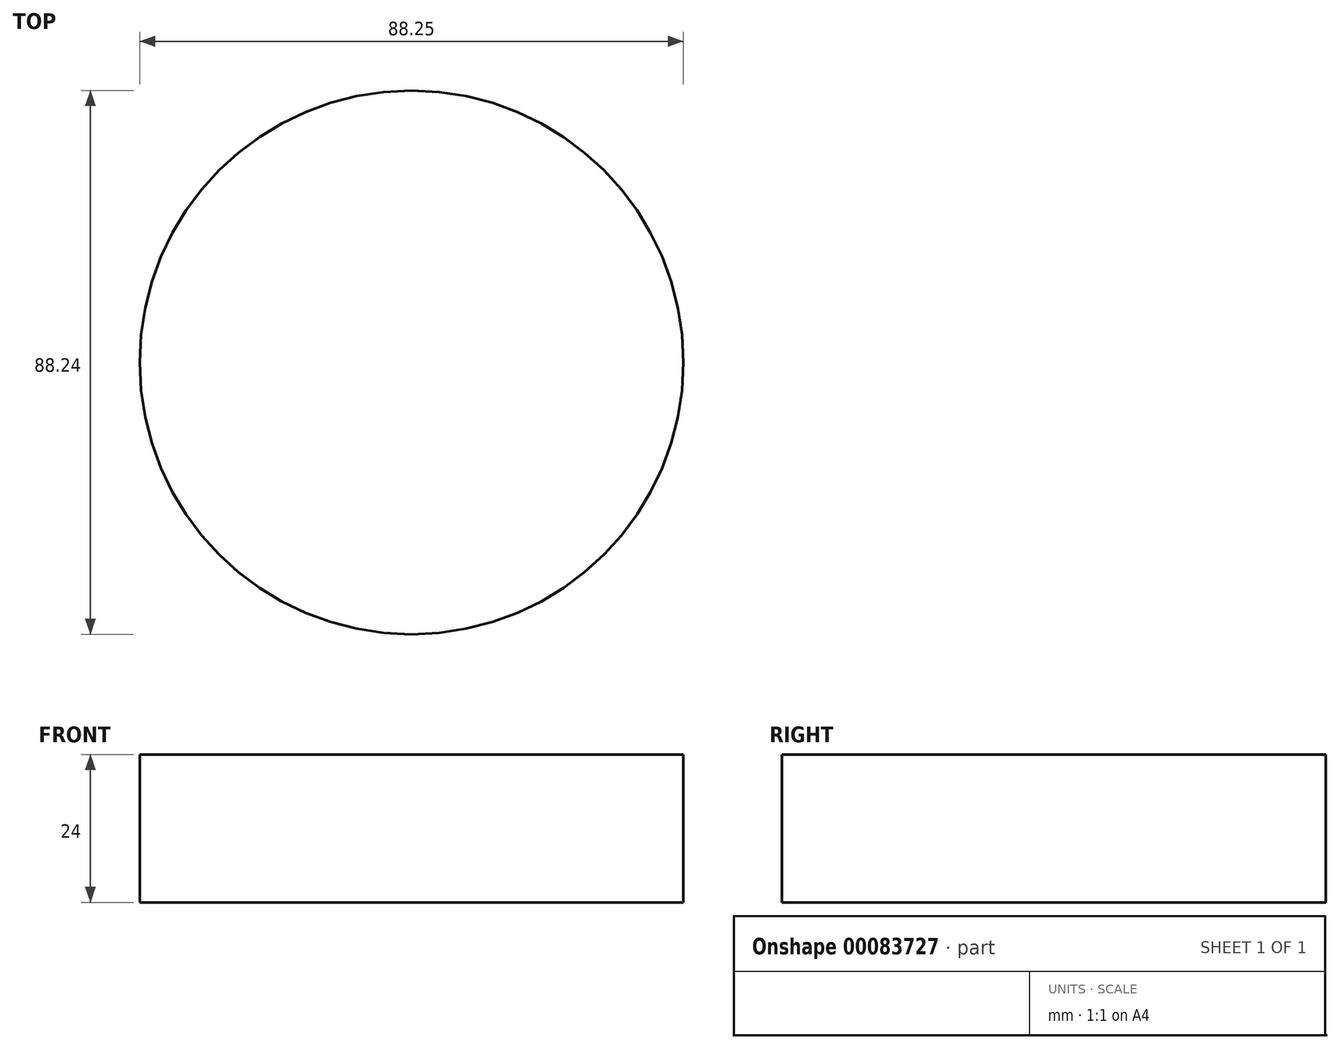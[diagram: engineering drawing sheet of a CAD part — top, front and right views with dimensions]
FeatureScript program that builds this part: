
annotation { "Feature Type Name" : "Feature", "Feature Type Description" : "" }
export const myFeature = defineFeature(function(context is Context, id is Id, definition is map)
    precondition{}
    {
        {
            var Q0;
            Q0=qCreatedBy(makeId("Top.planeOp"),FACE);
            var sketch = newSketch(context, id + "F0", { "sketchPlane" : qUnion([Q0])});
            skCircle(sketch, "E0", {"center": v(-3.94, 0) * mm, "radius": 44.12 * mm});
            skSolve(sketch);
        }
        {
            assignVariable(context, id + "F1", {"name" : "altezza", "anyValue" : 24});
        }
        {
            var Q0;
            Q0 = qSketchRegion(id + "F0", true);
            extrude(context, id + "F2", {"entities" : qUnion([Q0]), "depth" : (getVariable(context, 'altezza')) * mm});
        }
    });
